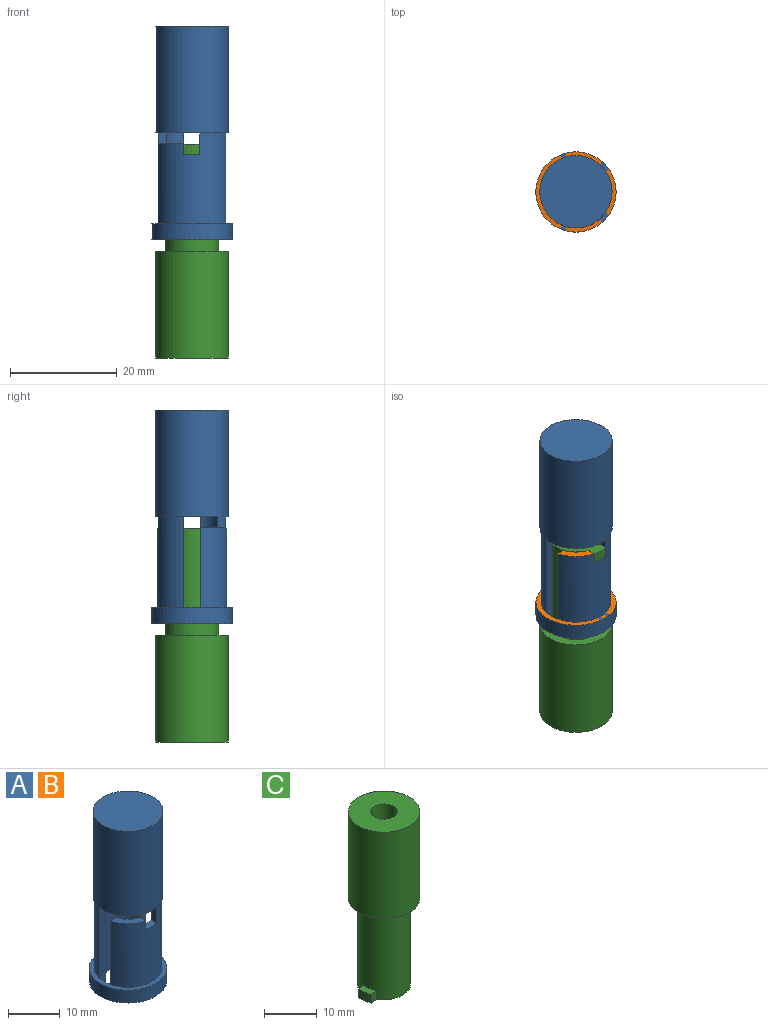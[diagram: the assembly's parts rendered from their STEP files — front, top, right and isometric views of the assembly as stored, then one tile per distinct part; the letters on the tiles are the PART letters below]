
ASSEMBLY  parts=3 mates=1
PART A: 28 faces, bbox 15x15x40 mm
  f0: plane 13.5x13.5mm, normal (0,0,-1), area 46.6mm2, adj f2,f4,f8,f9,f11,f12,f13,f21
  f1: plane 18x1.56mm, normal (0,1,0), area 28mm2, adj f2,f4,f5,f6,f18
  f2: cylinder r=6.5mm len=17mm, axis (0,0,-1), area 269.2mm2, adj f0,f1,f3,f5,f7,f8,f9,f20
  f3: plane 2x1.56mm, normal (1,0,0), area 3.1mm2, adj f2,f4,f5,f7
  f4: cylinder r=5mm len=22mm, axis (0,0,-1), area 525.7mm2, adj f0,f1,f3,f5,f6,f7,f8,f9
  f5: plane 4.82x4.82mm, normal (0,0,1), area 9mm2, adj f1,f2,f3,f4
  f6: plane 15x15mm, normal (0,0,-1), area 89.1mm2, adj f1,f4,f9,f10,f12,f14,f18,f19
  f7: plane 3x1.73mm, normal (0,0,1), area 4.6mm2, adj f2,f3,f4,f8
  f8: plane 4x1.56mm, normal (-1,0,0), area 6.2mm2, adj f0,f2,f4,f7
  f9: plane 20x1.56mm, normal (0,1,0), area 31.1mm2, adj f0,f2,f4,f6,f10
  f10: cylinder r=6.5mm len=3mm, axis (0,0,-1), area 9.1mm2, adj f6,f9,f14,f20
  f11: cylinder r=6.5mm len=17mm, axis (0,0,-1), area 269.2mm2, adj f0,f12,f13,f14,f15,f16,f17,f20
  f12: plane 20x1.56mm, normal (0,-1,0), area 31.1mm2, adj f0,f4,f6,f11,f18
  f13: plane 4x1.56mm, normal (1,0,0), area 6.2mm2, adj f0,f4,f11,f17
  f14: plane 18x1.56mm, normal (0,-1,0), area 28mm2, adj f4,f6,f10,f11,f16
  f15: plane 2x1.56mm, normal (-1,0,0), area 3.1mm2, adj f4,f11,f16,f17
  f16: plane 4.82x4.82mm, normal (0,0,1), area 9mm2, adj f4,f11,f14,f15
  f17: plane 3x1.73mm, normal (0,0,1), area 4.6mm2, adj f4,f11,f13,f15
  f18: cylinder r=6.5mm len=3mm, axis (0,0,-1), area 9.1mm2, adj f1,f6,f12,f20
  f19: cylinder r=7.5mm len=15mm, axis (0,0,-1), area 141.4mm2, adj f6,f20
  f20: plane 15x15mm, normal (0,0,1), area 44mm2, adj f2,f10,f11,f18,f19
  f21: cylinder r=6.75mm len=20mm, axis (0,0,-1), area 848.2mm2, adj f0,f22
  f22: plane 13.5x13.5mm, normal (0,0,1), area 143.1mm2, adj f21
  f23: plane 10x10mm, normal (0,0,-1), area 40.1mm2, adj f4,f24
  f24: cylinder r=3.5mm len=8mm, axis (0,0,-1), area 175.9mm2, adj f23,f25
  f25: plane 7x7mm, normal (0,0,-1), area 31.4mm2, adj f24,f26
  f26: cylinder r=1.5mm len=5mm, axis (0,0,-1), area 47.1mm2, adj f25,f27
  f27: plane 3x3mm, normal (0,0,-1), area 7.1mm2, adj f26
PART B: same geometry as A
PART C: 14 faces, bbox 13.5x13.5x40 mm
  f0: cylinder r=5mm len=20mm, axis (0,0,-1), area 616.1mm2, adj f3,f5,f6,f8,f9,f10,f12,f13
  f1: cylinder r=2.5mm len=40mm, axis (0,0,-1), area 628.3mm2, adj f2,f3
  f2: plane 13.5x13.5mm, normal (0,0,1), area 123.5mm2, adj f1,f4
  f3: plane 13x10mm, normal (0,0,-1), area 68mm2, adj f0,f1,f6,f7,f8,f10,f11,f12
  f4: cylinder r=6.75mm len=20mm, axis (0,0,1), area 848.2mm2, adj f2,f5
  f5: plane 13.5x13.5mm, normal (0,0,-1), area 64.6mm2, adj f0,f4
  f6: plane 2x1.53mm, normal (0.18,-0.98,0), area 3.1mm2, adj f0,f3,f7,f9
  f7: cylinder r=6.5mm len=2.95mm, axis (0,0,-1), area 6.1mm2, adj f3,f6,f8,f9
  f8: plane 2x1.53mm, normal (-0.18,0.98,0), area 3.1mm2, adj f0,f3,f7,f9
  f9: plane 3.23x2.08mm, normal (0,0,1), area 4.6mm2, adj f0,f6,f7,f8
  f10: plane 2x1.53mm, normal (-0.18,0.98,0), area 3.1mm2, adj f0,f3,f11,f13
  f11: cylinder r=6.5mm len=2.95mm, axis (0,0,-1), area 6.1mm2, adj f3,f10,f12,f13
  f12: plane 2x1.53mm, normal (0.18,-0.98,0), area 3.1mm2, adj f0,f3,f11,f13
  f13: plane 3.23x2.08mm, normal (0,0,1), area 4.6mm2, adj f0,f10,f11,f12
PLACE A t=(-14.36,-6.15,-16.8)mm fixed
PLACE B t=(-14.36,-6.15,-16.8)mm fixed
PLACE C rot(axis=(-0.77,0.64,0),180deg) t=(-14.36,-6.15,1.14)mm
MATE cylindrical C.f1 <-> B.f21  axis (0,0,-1) through (-14.36,-6.15,21.14)mm
